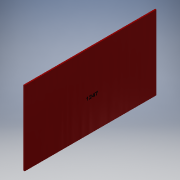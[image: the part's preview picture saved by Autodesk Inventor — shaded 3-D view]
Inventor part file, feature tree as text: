
AUTODESK INVENTOR PART (.ipt)
format: ipt  version: 2017 (Build 210142000, 142)  size: 691,712 bytes
history: native  units: in
note: dims shown in document units (in); Inventor stores cm internally (conversion verified against a paired STEP export)
features: sketch x24, extrude x18, plane x9, projected_geometry x6, loft x4, other x3, mirror x1, emboss x1, fillet x1
ambient origin geometry x8: Origin, YZ Plane, XZ Plane, XY Plane, X Axis, Y Axis, Z Axis, Center Point
bodies: Solid1 (feature_tree)
feature tree (67):
  sketch  "Sketch1"  dims[d0=0.7559in d1=0.7559in]
  plane  "Work Plane1"
  loft  "Loft1"
  extrude  "Extrusion1"  Depth=0.2in
  plane  "Work Plane4"
  loft  "Loft2"
  plane  "Work Plane5"
  loft  "Loft3"
  loft  "Loft4"
  extrude  "Extrusion2"  TaperAngle=0.0deg  [1 undecoded]
  plane  "Work Plane6"
  extrude  "Extrusion3"  Depth=1.0in
  extrude  "Extrusion4"  Depth=1.0651in
  extrude  "Extrusion5"  Depth=0.962in
  plane  "Work Plane7"
  extrude  "Extrusion6"  Depth=0.075in
  plane  "Work Plane8"
  other  "Work Axis1"
  plane  "Work Plane9"
  extrude  "Extrusion7"  Depth=0.06in
  mirror  "Mirror3"
  extrude  "Extrusion8"  Depth=0.05in
  plane  "Work Plane10"
  extrude  "Extrusion9"  Depth=0.0625in
  plane  "Work Plane11"
  extrude  "Extrusion10"  Depth=0.075in
  extrude  "Extrusion11"  TaperAngle=0.0deg  [1 undecoded]
  extrude  "Extrusion12"  Depth=0.2in
  extrude  "Extrusion13"  TaperAngle=0.0deg  [1 undecoded]
  emboss  "Emboss1"
  extrude  "Extrusion16"  Depth=0.01in
  extrude  "Extrusion17"  Depth=0.0344in
  extrude  "Extrusion18"  TaperAngle=60.0deg  [1 undecoded]
  fillet  "Fillet1"  [1 undecoded]
  extrude  "Extrusion20"  Depth=0.05in
  extrude  "Extrusion21"  Depth=0.05in
  sketch  "Sketch2"  dims[d2=0.9963in d3=0.2in]
  sketch  "Sketch3"  dims[d4=0.5in d6=0.08in]
  sketch  "Sketch4"  dims[d7=0.55in d8=150.0deg]
  other  "Edges1"
  sketch  "Sketch5"  dims[d9=150.0deg d14=0.33in]
  projected_geometry  "Projected Loop1"
  other  "Edges2"
  sketch  "Sketch6"  dims[d15=0.66in d18=0.0in d19=90.0deg]
  sketch  "Sketch7"  dims[d20=0.0in d21=90.0deg d22=1.0in]
  sketch  "Sketch8"  dims[d26=1.0651in d28=1.0651in]
  sketch  "Sketch9"  dims[d29=0.0in d30=0.962in]
  sketch  "Sketch10"  dims[d31=0.962in d32=0.075in]
  sketch  "Sketch11"  dims[d33=0.15in d34=0.06in]
  sketch  "Sketch12"  dims[d35=0.1in d36=0.05in]
  sketch  "Sketch13"  dims[d37=0.45in d38=0.0in d39=0.0625in]
  projected_geometry  "Projected Loop2"
  projected_geometry  "Projected Loop3"
  sketch  "Sketch14"  dims[d40=0.01in d41=0.075in]
  projected_geometry  "Projected Loop4"
  sketch  "Sketch15"  dims[d42=0.01in d43=0.0in d44=90.0deg]
  sketch  "Sketch16"  dims[d45=0.0in d46=90.0deg d47=0.2in]
  sketch  "Sketch17"  dims[d48=0.07in d49=0.0in d50=90.0deg]
  sketch  "Sketch18"  dims[d51=0.0in d52=90.0deg d53=0.01in]
  sketch  "Sketch19"  dims[d54=0.01in d55=0.0344in]
  sketch  "Sketch23"  dims[d56=150.0deg d57=60.0deg d58=150.0deg]
  projected_geometry  "Projected Loop6"
  sketch  "Sketch24"  dims[d59=0.7in d60=0.05in]
  sketch  "Sketch25"  dims[d61=0.05in d62=0.05in d63=0.05in]
  sketch  "Sketch27"  dims[d64=0.05in]
  sketch  "Sketch28"  dims[d65=0.01in d66=0.0in d67=90.0deg d68=0.0in d69=90.0deg d70=0.1in d71=0.4in d72=0.15in d73=0.05in d74=0.0in d75=0.02in d77=0.15in d78=0.02in d79=0.1in d80=0.1in d81=0.1in d82=0.02in d83=0.15in d84=0.05in d85=0.0in d86=0.045in d87=0.0in d88=0.025in d89=0.0in d90=0.02in d91=0.02in d92=0.005in d93=0.0in d94=90.0deg d95=0.4466in d96=1.0in d97=0.0in d98=1.0in d99=0.0in d100=0.6528in d101=0.0in d102=0.0in d103=1.0in d104=0.0in d106=90.0deg d107=1.0in d108=0.0in d109=1.65in d110=0.1in d111=0.1in d112=0.0in d113=0.1in d114=0.075in d115=0.0in d116=0.05in d117=0.0in d123=0.84in d124=0.8in d125=0.0in d126=0.0in d127=1.0in d128=0.0in d130=0.15in d131=-0.0206in d135=0.2in d136=0.05in d137=0.1in d140=0.05in d141=0.1in d142=0.0in d143=1.0in d144=0.0in]
  projected_geometry  "Projected Loop9"
note: 5 required parameter values undecoded (feature->parameter linkage not recoverable at this tier; creation-order binding heuristic only, values carry confidence <= 0.55)
